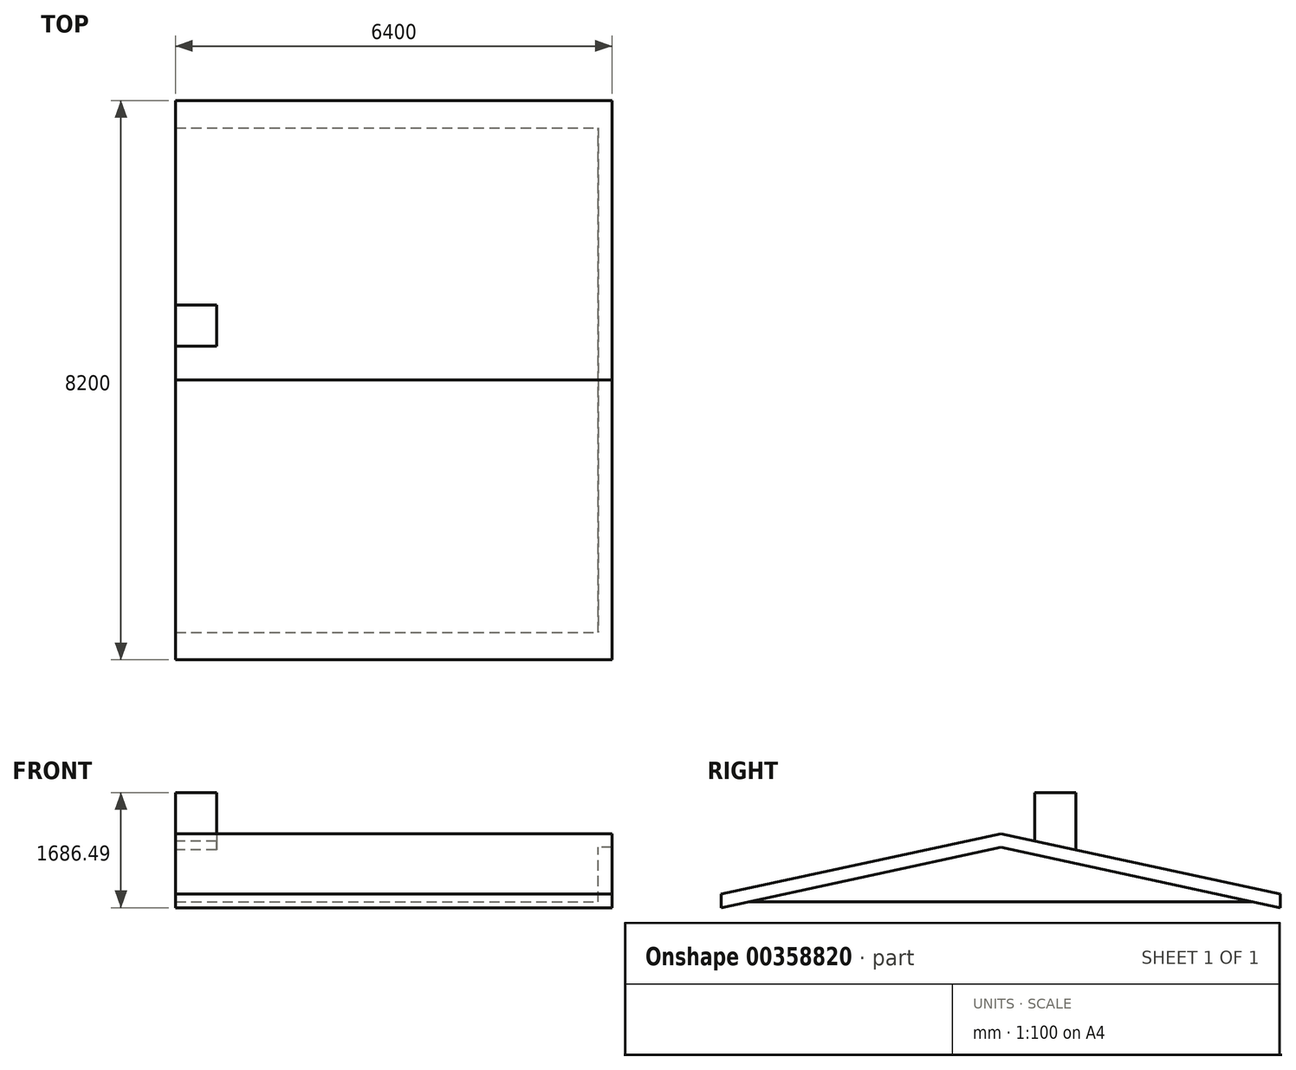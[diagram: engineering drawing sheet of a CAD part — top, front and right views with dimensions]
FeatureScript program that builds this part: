
annotation { "Feature Type Name" : "Feature", "Feature Type Description" : "" }
export const myFeature = defineFeature(function(context is Context, id is Id, definition is map)
    precondition{}
    {
        {
            var Q0;
            Q0=qCreatedBy(makeId("Right.planeOp"),FACE);
            var sketch = newSketch(context, id + "F0", { "sketchPlane" : qUnion([Q0])});
            skLineSegment(sketch, "E0", {"start": v(0, 0) * mm, "end": v(7400, 0) * mm});
            skLineSegment(sketch, "E1", {"start": v(7400, 0) * mm, "end": v(7800, -86.49) * mm});
            skLineSegment(sketch, "E2", {"start": v(7800, 113.51) * mm, "end": v(3700, 1000) * mm});
            skLineSegment(sketch, "E3", {"start": v(3700, 1000) * mm, "end": v(-400, 113.51) * mm});
            skLineSegment(sketch, "E4", {"start": v(-400, -86.49) * mm, "end": v(0, 0) * mm});
            skLineSegment(sketch, "E5", {"start": v(3700, 0) * mm, "end": v(3700, 1000) * mm, "construction": true});
            skLineSegment(sketch, "E6", {"start": v(-400, -86.49) * mm, "end": v(-400, 113.51) * mm});
            skLineSegment(sketch, "E7", {"start": v(7800, -86.49) * mm, "end": v(7800, 113.51) * mm});
            skSolve(sketch);
        }
        {
            var Q0;
            Q0 = qSketchRegion(id + "F0", true);
            extrude(context, id + "F1", {"entities" : qUnion([Q0]), "oppositeDirection" : true, "depth" : 6200 * mm});
        }
        {
            var Q0;
            Q0=makeQuery(id+"F1.opExtrude","CAP_FACE",FACE,{"disambiguationData":[OSD([sQuery(id+"F0.wireOp",EDGE,"E0"),sQuery(id+"F0.wireOp",EDGE,"E1"),sQuery(id+"F0.wireOp",EDGE,"E2"),sQuery(id+"F0.wireOp",EDGE,"E3"),sQuery(id+"F0.wireOp",EDGE,"E4"),sQuery(id+"F0.wireOp",EDGE,"E6"),sQuery(id+"F0.wireOp",EDGE,"E7")])],"isStart":true});
            var sketch = newSketch(context, id + "F2", { "sketchPlane" : qUnion([Q0])});
            skLineSegment(sketch, "E8.0", {"start": v(3700, 1000) * mm, "end": v(-400, 113.51) * mm});
            skLineSegment(sketch, "E9.0", {"start": v(-400, -86.49) * mm, "end": v(-400, 113.51) * mm});
            skLineSegment(sketch, "E10.0", {"start": v(7800, 113.51) * mm, "end": v(3700, 1000) * mm});
            skLineSegment(sketch, "E11.0", {"start": v(7800, -86.49) * mm, "end": v(7800, 113.51) * mm});
            skLineSegment(sketch, "E12.0", {"start": v(3700, 800) * mm, "end": v(-400, -86.49) * mm});
            skLineSegment(sketch, "E12.1", {"start": v(7800, -86.49) * mm, "end": v(3700, 800) * mm});
            skSolve(sketch);
        }
        {
            var Q0;
            Q0 = qSketchRegion(id + "F2", true);
            extrude(context, id + "F3", {"entities" : qUnion([Q0]), "operationType" : NewBodyOperationType.ADD, "depth" : 200 * mm});
        }
        {
            var Q0;
            Q0=makeQuery(id+"F1.opExtrude","SWEPT_FACE",FACE,{"disambiguationData":[OSD([sQuery(id+"F0.wireOp",EDGE,"E0")])]});
            var sketch = newSketch(context, id + "F4", { "sketchPlane" : qUnion([Q0])});
            skLineSegment(sketch, "E13.bottom", {"start": v(-6200, -4200) * mm, "end": v(-5600, -4200) * mm});
            skLineSegment(sketch, "E13.top", {"start": v(-6200, -4800) * mm, "end": v(-5600, -4800) * mm});
            skLineSegment(sketch, "E13.left", {"start": v(-6200, -4200) * mm, "end": v(-6200, -4800) * mm});
            skLineSegment(sketch, "E13.right", {"start": v(-5600, -4200) * mm, "end": v(-5600, -4800) * mm});
            skSolve(sketch);
        }
        {
            var Q0;
            Q0 = qSketchRegion(id + "F4", true);
            extrude(context, id + "F5", {"entities" : qUnion([Q0]), "operationType" : NewBodyOperationType.ADD, "oppositeDirection" : true, "depth" : 1600 * mm});
        }
    });
